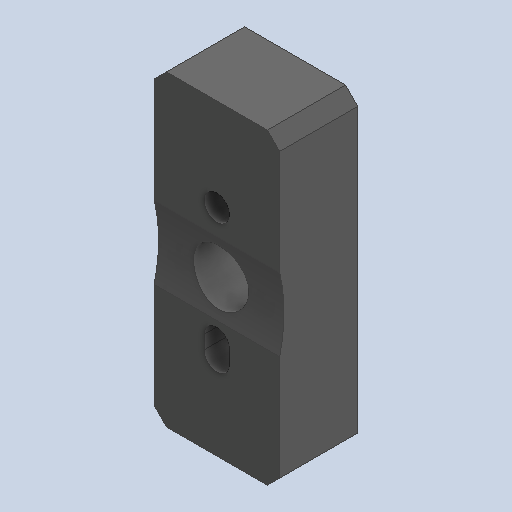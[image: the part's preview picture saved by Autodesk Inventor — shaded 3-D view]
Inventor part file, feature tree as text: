
AUTODESK INVENTOR PART (.ipt)
format: ipt  version: 2024.2 (Build 282272000, 272)  size: 164,352 bytes
history: native  units: in
note: dims shown in document units (in); Inventor stores cm internally (conversion verified against a paired STEP export)
features: extrude x4, hole x2, chamfer x1
ambient origin geometry x8: Origin, YZ Plane, XZ Plane, XY Plane, X Axis, Y Axis, Z Axis, Center Point
bodies: Solid1 (feature_tree)
feature tree (7):
  extrude  "Extrusion1"  Depth=0.4921in
  extrude  "Extrusion2"  Depth=0.25in TaperAngle=0.0deg
  hole  "Hole1"  [1 undecoded]
  hole  "Hole2"  [1 undecoded]
  extrude  "Extrusion3"  Depth=0.4921in
  chamfer  "Chamfer1"  [1 undecoded]
  extrude  "Extrusion4"  Depth=0.0492in TaperAngle=0.0deg
note: 3 required parameter values undecoded (feature->parameter linkage not recoverable at this tier; creation-order binding heuristic only, values carry confidence <= 0.55)
